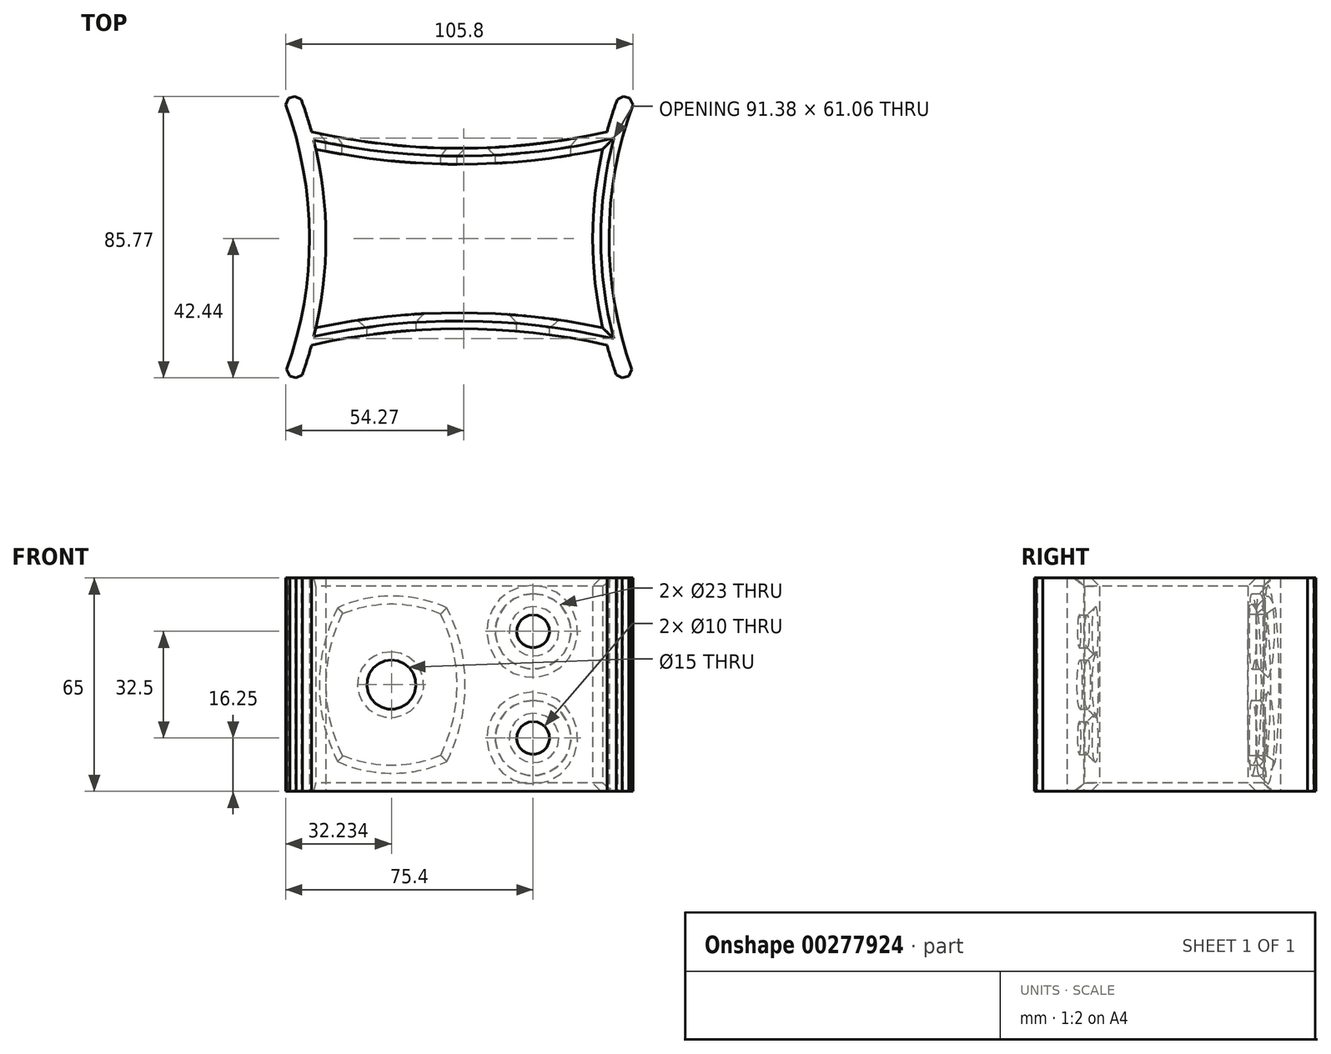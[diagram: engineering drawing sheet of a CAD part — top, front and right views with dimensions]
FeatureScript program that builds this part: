
annotation { "Feature Type Name" : "Feature", "Feature Type Description" : "" }
export const myFeature = defineFeature(function(context is Context, id is Id, definition is map)
    precondition{}
    {
        {
            var Q0;
            Q0=qCreatedBy(makeId("Top.planeOp"),FACE);
            var sketch = newSketch(context, id + "F0", { "sketchPlane" : qUnion([Q0])});
            skLineSegment(sketch, "E0.bottom", {"start": v(0, 0) * mm, "end": v(90, 0) * mm, "construction": true});
            skLineSegment(sketch, "E0.top", {"start": v(0, -5) * mm, "end": v(90, -5) * mm, "construction": true});
            skLineSegment(sketch, "E0.left", {"start": v(0, 0) * mm, "end": v(0, -5) * mm});
            skLineSegment(sketch, "E0.right", {"start": v(90, 0) * mm, "end": v(90, -5) * mm});
            skArc(sketch, "E1", {"start": v(0, 0) * mm, "mid": v(45, -5) * mm, "end": v(90, 0) * mm});
            skArc(sketch, "E2", {"start": v(0, -5) * mm, "mid": v(45, -9.88) * mm, "end": v(90, -5) * mm});
            skLineSegment(sketch, "E3", {"start": v(0, 0) * mm, "end": v(0, -65) * mm, "construction": true});
            skLineSegment(sketch, "E4", {"start": v(0, -32.5) * mm, "end": v(-19.4, -32.5) * mm});
            skLineSegment(sketch, "E5.MirrorCS", {"start": v(90, -65) * mm, "end": v(90, -60) * mm});
            skLineSegment(sketch, "E6.MirrorCS", {"start": v(0, -65) * mm, "end": v(0, -60) * mm});
            skArc(sketch, "E7.MirrorCS", {"start": v(0, -60) * mm, "mid": v(45, -55.12) * mm, "end": v(90, -60) * mm});
            skArc(sketch, "E8.MirrorCS", {"start": v(0, -65) * mm, "mid": v(45, -60) * mm, "end": v(90, -65) * mm});
            skArc(sketch, "E9", {"start": v(98.46, 9.78) * mm, "mid": v(90.63, -32.05) * mm, "end": v(98.14, -73.94) * mm});
            skLineSegment(sketch, "E10", {"start": v(90, 0) * mm, "end": v(90, -65) * mm, "construction": true});
            skLineSegment(sketch, "E11", {"start": v(90, -32.5) * mm, "end": v(208.75, -32.5) * mm, "construction": true});
            skArc(sketch, "E12.0", {"start": v(93.66, 11.24) * mm, "mid": v(85.63, -32.01) * mm, "end": v(93.32, -75.33) * mm});
            skLineSegment(sketch, "E13", {"start": v(93.32, -75.33) * mm, "end": v(98.14, -73.94) * mm});
            skLineSegment(sketch, "E14", {"start": v(98.46, 9.78) * mm, "end": v(93.66, 11.24) * mm});
            skLineSegment(sketch, "E15", {"start": v(45, 0) * mm, "end": v(45, 27.4) * mm});
            skArc(sketch, "E16.MirrorCS", {"start": v(-8.46, 9.78) * mm, "mid": v(-0.63, -32.05) * mm, "end": v(-8.14, -73.94) * mm});
            skArc(sketch, "E17.MirrorCS", {"start": v(-3.66, 11.24) * mm, "mid": v(4.37, -32.01) * mm, "end": v(-3.32, -75.33) * mm});
            skLineSegment(sketch, "E18.MirrorCS", {"start": v(-8.46, 9.78) * mm, "end": v(-3.66, 11.24) * mm});
            skLineSegment(sketch, "E19.MirrorCS", {"start": v(-3.32, -75.33) * mm, "end": v(-8.14, -73.94) * mm});
            skSolve(sketch);
        }
        {
            var Q0;
            Q0 = qSketchRegion(id + "F0", true);
            extrude(context, id + "F1", {"entities" : qUnion([Q0]), "depth" : 65 * mm});
        }
        {
            var Q0;
            Q0=qCreatedBy(makeId("Front.planeOp"),FACE);
            var sketch = newSketch(context, id + "F2", { "sketchPlane" : qUnion([Q0])});
            skLineSegment(sketch, "E20.0.0", {"start": v(90, 0) * mm, "end": v(0, 0) * mm, "construction": true});
            skLineSegment(sketch, "E20.0.1", {"start": v(0, 0) * mm, "end": v(0, 65) * mm, "construction": true});
            skLineSegment(sketch, "E20.0.2", {"start": v(0, 65) * mm, "end": v(90, 65) * mm, "construction": true});
            skLineSegment(sketch, "E20.0.3", {"start": v(90, 65) * mm, "end": v(90, 0) * mm, "construction": true});
            skLineSegment(sketch, "E21", {"start": v(45, 0) * mm, "end": v(45, 65) * mm, "construction": true});
            skLineSegment(sketch, "E22", {"start": v(45, 65) * mm, "end": v(90, 0) * mm, "construction": true});
            skLineSegment(sketch, "E23", {"start": v(48.67, 65) * mm, "end": v(0, 0) * mm, "construction": true});
            skLineSegment(sketch, "E24.bottom", {"start": v(39.33, 11) * mm, "end": v(9.33, 11) * mm, "construction": true});
            skLineSegment(sketch, "E24.top", {"start": v(39.33, 54) * mm, "end": v(9.33, 54) * mm, "construction": true});
            skLineSegment(sketch, "E24.left", {"start": v(39.33, 11) * mm, "end": v(39.33, 54) * mm, "construction": true});
            skLineSegment(sketch, "E24.right", {"start": v(9.33, 11) * mm, "end": v(9.33, 54) * mm, "construction": true});
            skPoint(sketch, "E24.middle", {"position": v(24.33, 32.5) * mm});
            skArc(sketch, "E25", {"start": v(39.33, 11) * mm, "mid": v(44.33, 32.5) * mm, "end": v(39.33, 54) * mm});
            skLineSegment(sketch, "E26", {"start": v(24.33, 11) * mm, "end": v(24.33, 54) * mm, "construction": true});
            skArc(sketch, "E27.MirrorCS", {"start": v(9.33, 11) * mm, "mid": v(4.33, 32.5) * mm, "end": v(9.33, 54) * mm});
            skArc(sketch, "E28", {"start": v(9.33, 11) * mm, "mid": v(24.33, 8) * mm, "end": v(39.33, 11) * mm});
            skArc(sketch, "E29", {"start": v(39.33, 54) * mm, "mid": v(24.33, 57) * mm, "end": v(9.33, 54) * mm});
            skLineSegment(sketch, "E30", {"start": v(67.5, 32.5) * mm, "end": v(90, 32.5) * mm, "construction": true});
            skLineSegment(sketch, "E31", {"start": v(67.5, 32.5) * mm, "end": v(67.5, 0) * mm, "construction": true});
            skCircle(sketch, "E32", {"center": v(67.5, 16.25) * mm, "radius": 11.5 * mm});
            skCircle(sketch, "E33.MirrorC", {"center": v(67.5, 48.75) * mm, "radius": 11.5 * mm});
            skSolve(sketch);
        }
        {
            var Q0;
            Q0 = qSketchRegion(id + "F2", true);
            extrude(context, id + "F3", {"entities" : qUnion([Q0]), "operationType" : NewBodyOperationType.REMOVE, "depth" : 25 * mm});
        }
        {
            var Q0;
            Q0=qCreatedBy(makeId("Front.planeOp"),FACE);
            var sketch = newSketch(context, id + "F4", { "sketchPlane" : qUnion([Q0])});
            skLineSegment(sketch, "E34.0", {"start": v(48.67, 65) * mm, "end": v(0, 0) * mm, "construction": true});
            skLineSegment(sketch, "E34.1", {"start": v(67.5, 32.5) * mm, "end": v(67.5, 0) * mm, "construction": true});
            skLineSegment(sketch, "E34.2", {"start": v(67.5, 32.5) * mm, "end": v(90, 32.5) * mm, "construction": true});
            skCircle(sketch, "E35", {"center": v(24.33, 32.5) * mm, "radius": 7.5 * mm});
            skCircle(sketch, "E36", {"center": v(67.5, 16.25) * mm, "radius": 5 * mm});
            skCircle(sketch, "E37.MirrorC", {"center": v(67.5, 48.75) * mm, "radius": 5 * mm});
            skSolve(sketch);
        }
        {
            var Q0;
            Q0 = qSketchRegion(id + "F4", true);
            extrude(context, id + "F5", {"entities" : qUnion([Q0]), "operationType" : NewBodyOperationType.REMOVE, "depth" : 80 * mm});
        }
        {
            var Q0;
            Q0=makeQuery(id+"F1.opExtrude","SWEPT_EDGE",EDGE,{"disambiguationData":[OSD([sQuery(id+"F0.wireOp",EDGE,"E16.MirrorCS"),sQuery(id+"F0.wireOp",EDGE,"E18.MirrorCS")])]});
            var Q1;
            Q1=makeQuery(id+"F1.opExtrude","SWEPT_EDGE",EDGE,{"disambiguationData":[OSD([sQuery(id+"F0.wireOp",EDGE,"E17.MirrorCS"),sQuery(id+"F0.wireOp",EDGE,"E18.MirrorCS")])]});
            var Q2;
            Q2=makeQuery(id+"F1.opExtrude","SWEPT_EDGE",EDGE,{"disambiguationData":[OSD([sQuery(id+"F0.wireOp",EDGE,"E12.0"),sQuery(id+"F0.wireOp",EDGE,"E14")])]});
            var Q3;
            Q3=makeQuery(id+"F1.opExtrude","SWEPT_EDGE",EDGE,{"disambiguationData":[OSD([sQuery(id+"F0.wireOp",EDGE,"E9"),sQuery(id+"F0.wireOp",EDGE,"E14")])]});
            var Q4;
            Q4=makeQuery(id+"F1.opExtrude","SWEPT_EDGE",EDGE,{"disambiguationData":[OSD([sQuery(id+"F0.wireOp",EDGE,"E17.MirrorCS"),sQuery(id+"F0.wireOp",EDGE,"E19.MirrorCS")])]});
            var Q5;
            Q5=makeQuery(id+"F1.opExtrude","SWEPT_EDGE",EDGE,{"disambiguationData":[OSD([sQuery(id+"F0.wireOp",EDGE,"E16.MirrorCS"),sQuery(id+"F0.wireOp",EDGE,"E19.MirrorCS")])]});
            var Q6;
            Q6=makeQuery(id+"F1.opExtrude","SWEPT_EDGE",EDGE,{"disambiguationData":[OSD([sQuery(id+"F0.wireOp",EDGE,"E12.0"),sQuery(id+"F0.wireOp",EDGE,"E13")])]});
            var Q7;
            Q7=makeQuery(id+"F1.opExtrude","SWEPT_EDGE",EDGE,{"disambiguationData":[OSD([sQuery(id+"F0.wireOp",EDGE,"E9"),sQuery(id+"F0.wireOp",EDGE,"E13")])]});
            chamfer(context, id + "F6", {"entities" : qUnion([Q0, Q1, Q2, Q3, Q4, Q5, Q6, Q7]), "width" : 1.5 * mm, "tangentPropagation" : true});
        }
        {
            var Q0;
            Q0=makeQuery(id+"F1.opExtrude","CAP_EDGE",EDGE,{"disambiguationData":[OSD([sQuery(id+"F0.wireOp",EDGE,"E2")])],"isStart":false});
            var Q1;
            {var subQ0=sQuery(id+"F0.wireOp",EDGE,"E17.MirrorCS");Q1=makeQuery(id+"F1.opExtrude","CAP_EDGE",EDGE,{"disambiguationData":[OSD([subQ0]),TDD([makeQuery(id+"F0.imprint","IMPRINT",EDGE,{"disambiguationData":[TD([[makeQuery(id+"F0.imprint","INTERSECT",VERTEX,{"derivedFrom":[sQuery(id+"F0.wireOp",EDGE,"E2"),subQ0]}),-1.0]])],"derivedFrom":subQ0})])],"isStart":false});}
            var Q2;
            Q2=makeQuery(id+"F1.opExtrude","CAP_EDGE",EDGE,{"disambiguationData":[OSD([sQuery(id+"F0.wireOp",EDGE,"E7.MirrorCS")])],"isStart":false});
            var Q3;
            {var subQ0=sQuery(id+"F0.wireOp",EDGE,"E12.0");Q3=makeQuery(id+"F1.opExtrude","CAP_EDGE",EDGE,{"disambiguationData":[OSD([subQ0]),TDD([makeQuery(id+"F0.imprint","IMPRINT",EDGE,{"disambiguationData":[TD([[makeQuery(id+"F0.imprint","INTERSECT",VERTEX,{"derivedFrom":[sQuery(id+"F0.wireOp",EDGE,"E2"),subQ0]}),-1.0]])],"derivedFrom":subQ0})])],"isStart":false});}
            var Q4;
            Q4=makeQuery(id+"F1.opExtrude","CAP_EDGE",EDGE,{"disambiguationData":[OSD([sQuery(id+"F0.wireOp",EDGE,"E2")])],"isStart":true});
            var Q5;
            {var subQ0=sQuery(id+"F0.wireOp",EDGE,"E12.0");Q5=makeQuery(id+"F1.opExtrude","CAP_EDGE",EDGE,{"disambiguationData":[OSD([subQ0]),TDD([makeQuery(id+"F0.imprint","IMPRINT",EDGE,{"disambiguationData":[TD([[makeQuery(id+"F0.imprint","INTERSECT",VERTEX,{"derivedFrom":[sQuery(id+"F0.wireOp",EDGE,"E2"),subQ0]}),-1.0]])],"derivedFrom":subQ0})])],"isStart":true});}
            var Q6;
            Q6=makeQuery(id+"F1.opExtrude","CAP_EDGE",EDGE,{"disambiguationData":[OSD([sQuery(id+"F0.wireOp",EDGE,"E7.MirrorCS")])],"isStart":true});
            var Q7;
            {var subQ0=sQuery(id+"F0.wireOp",EDGE,"E17.MirrorCS");Q7=makeQuery(id+"F1.opExtrude","CAP_EDGE",EDGE,{"disambiguationData":[OSD([subQ0]),TDD([makeQuery(id+"F0.imprint","IMPRINT",EDGE,{"disambiguationData":[TD([[makeQuery(id+"F0.imprint","INTERSECT",VERTEX,{"derivedFrom":[sQuery(id+"F0.wireOp",EDGE,"E2"),subQ0]}),-1.0]])],"derivedFrom":subQ0})])],"isStart":true});}
            chamfer(context, id + "F7", {"entities" : qUnion([Q0, Q1, Q2, Q3, Q4, Q5, Q6, Q7]), "width" : 2.5 * mm, "tangentPropagation" : true});
        }
        {
            var Q0;
            Q0=makeQuery(id+"F3.boolean.opBoolean","INTERSECT",EDGE,{"derivedFrom":[makeQuery(id+"F1.opExtrude","SWEPT_FACE",FACE,{"disambiguationData":[OSD([sQuery(id+"F0.wireOp",EDGE,"E1")])]}),makeQuery(id+"F3.opExtrude","SWEPT_FACE",FACE,{"disambiguationData":[OSD([sQuery(id+"F2.wireOp",EDGE,"E28")])]})]});
            var Q1;
            Q1=makeQuery(id+"F3.boolean.opBoolean","INTERSECT",EDGE,{"derivedFrom":[makeQuery(id+"F1.opExtrude","SWEPT_FACE",FACE,{"disambiguationData":[OSD([sQuery(id+"F0.wireOp",EDGE,"E1")])]}),makeQuery(id+"F3.opExtrude","SWEPT_FACE",FACE,{"disambiguationData":[OSD([sQuery(id+"F2.wireOp",EDGE,"E25")])]})]});
            var Q2;
            Q2=makeQuery(id+"F3.boolean.opBoolean","INTERSECT",EDGE,{"derivedFrom":[makeQuery(id+"F1.opExtrude","SWEPT_FACE",FACE,{"disambiguationData":[OSD([sQuery(id+"F0.wireOp",EDGE,"E1")])]}),makeQuery(id+"F3.opExtrude","SWEPT_FACE",FACE,{"disambiguationData":[OSD([sQuery(id+"F2.wireOp",EDGE,"E27.MirrorCS")])]})]});
            var Q3;
            Q3=makeQuery(id+"F3.boolean.opBoolean","INTERSECT",EDGE,{"derivedFrom":[makeQuery(id+"F1.opExtrude","SWEPT_FACE",FACE,{"disambiguationData":[OSD([sQuery(id+"F0.wireOp",EDGE,"E1")])]}),makeQuery(id+"F3.opExtrude","SWEPT_FACE",FACE,{"disambiguationData":[OSD([sQuery(id+"F2.wireOp",EDGE,"E29")])]})]});
            var Q4;
            Q4=makeQuery(id+"F3.boolean.opBoolean","INTERSECT",EDGE,{"derivedFrom":[makeQuery(id+"F1.opExtrude","SWEPT_FACE",FACE,{"disambiguationData":[OSD([sQuery(id+"F0.wireOp",EDGE,"E1")])]}),makeQuery(id+"F3.opExtrude","SWEPT_FACE",FACE,{"disambiguationData":[OSD([sQuery(id+"F2.wireOp",EDGE,"E32")])]})]});
            var Q5;
            Q5=makeQuery(id+"F3.boolean.opBoolean","INTERSECT",EDGE,{"derivedFrom":[makeQuery(id+"F1.opExtrude","SWEPT_FACE",FACE,{"disambiguationData":[OSD([sQuery(id+"F0.wireOp",EDGE,"E1")])]}),makeQuery(id+"F3.opExtrude","SWEPT_FACE",FACE,{"disambiguationData":[OSD([sQuery(id+"F2.wireOp",EDGE,"E33.MirrorC")])]})]});
            var Q6;
            Q6=makeQuery(id+"F5.boolean.opBoolean","INTERSECT",EDGE,{"derivedFrom":[makeQuery(id+"F1.opExtrude","SWEPT_FACE",FACE,{"disambiguationData":[OSD([sQuery(id+"F0.wireOp",EDGE,"E7.MirrorCS")])]}),makeQuery(id+"F5.opExtrude","SWEPT_FACE",FACE,{"disambiguationData":[OSD([sQuery(id+"F4.wireOp",EDGE,"E35")])]})]});
            var Q7;
            Q7=makeQuery(id+"F5.boolean.opBoolean","INTERSECT",EDGE,{"derivedFrom":[makeQuery(id+"F1.opExtrude","SWEPT_FACE",FACE,{"disambiguationData":[OSD([sQuery(id+"F0.wireOp",EDGE,"E7.MirrorCS")])]}),makeQuery(id+"F5.opExtrude","SWEPT_FACE",FACE,{"disambiguationData":[OSD([sQuery(id+"F4.wireOp",EDGE,"E36")])]})]});
            var Q8;
            Q8=makeQuery(id+"F5.boolean.opBoolean","INTERSECT",EDGE,{"derivedFrom":[makeQuery(id+"F1.opExtrude","SWEPT_FACE",FACE,{"disambiguationData":[OSD([sQuery(id+"F0.wireOp",EDGE,"E7.MirrorCS")])]}),makeQuery(id+"F5.opExtrude","SWEPT_FACE",FACE,{"disambiguationData":[OSD([sQuery(id+"F4.wireOp",EDGE,"E37.MirrorC")])]})]});
            chamfer(context, id + "F8", {"entities" : qUnion([Q0, Q1, Q2, Q3, Q4, Q5, Q6, Q7, Q8]), "width" : 2.5 * mm, "tangentPropagation" : true});
        }
    });
